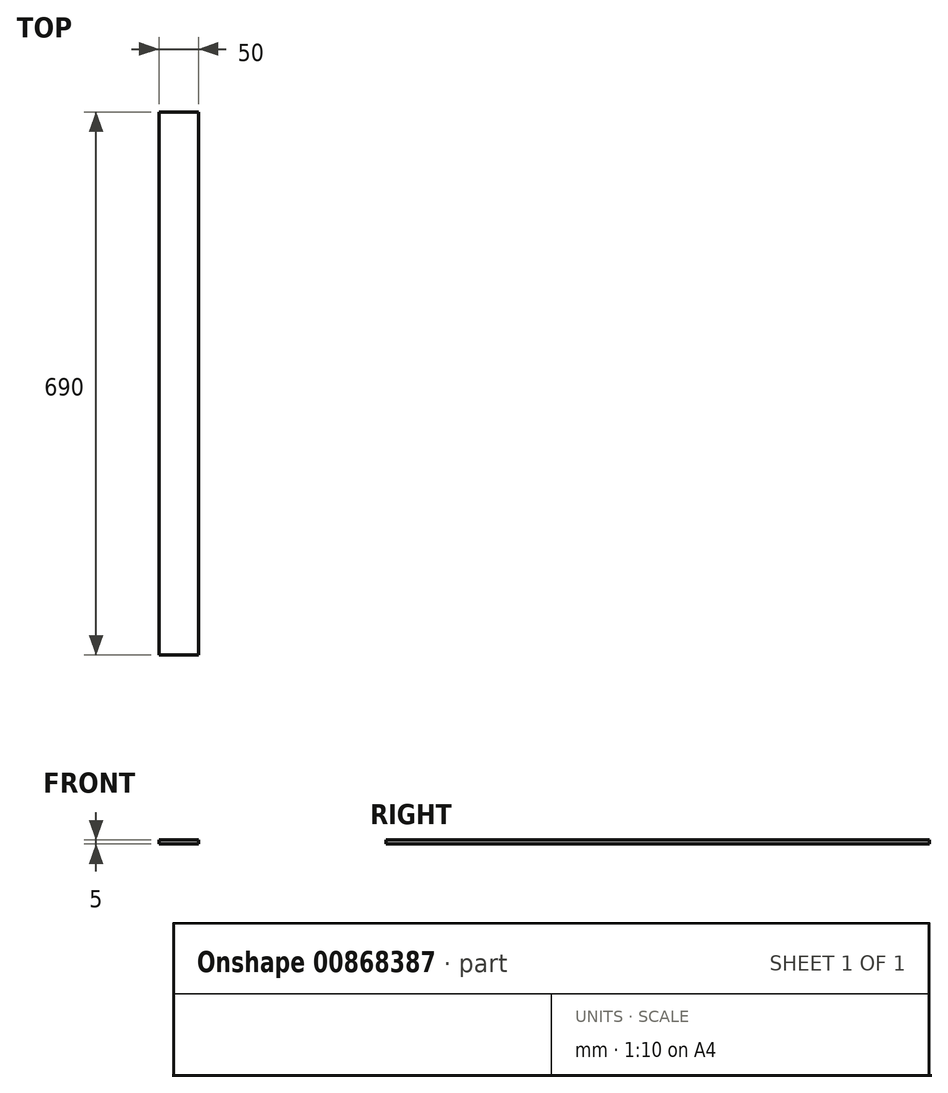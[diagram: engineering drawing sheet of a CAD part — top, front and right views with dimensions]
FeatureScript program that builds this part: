
annotation { "Feature Type Name" : "Feature", "Feature Type Description" : "" }
export const myFeature = defineFeature(function(context is Context, id is Id, definition is map)
    precondition{}
    {
        {
            var Q0;
            Q0=qCreatedBy(makeId("Top.planeOp"),FACE);
            var sketch = newSketch(context, id + "F0", { "sketchPlane" : qUnion([Q0])});
            skLineSegment(sketch, "E0.bottom", {"start": v(0, 0) * mm, "end": v(-50, 0) * mm});
            skLineSegment(sketch, "E0.top", {"start": v(0, 690) * mm, "end": v(-50, 690) * mm});
            skLineSegment(sketch, "E0.left", {"start": v(0, 0) * mm, "end": v(0, 690) * mm});
            skLineSegment(sketch, "E0.right", {"start": v(-50, 0) * mm, "end": v(-50, 690) * mm});
            skSolve(sketch);
        }
        {
            var Q0;
            Q0 = qSketchRegion(id + "F0", true);
            extrude(context, id + "F1", {"entities" : qUnion([Q0]), "depth" : 5 * mm, "offsetDistance" : 25 * mm});
        }
    });
